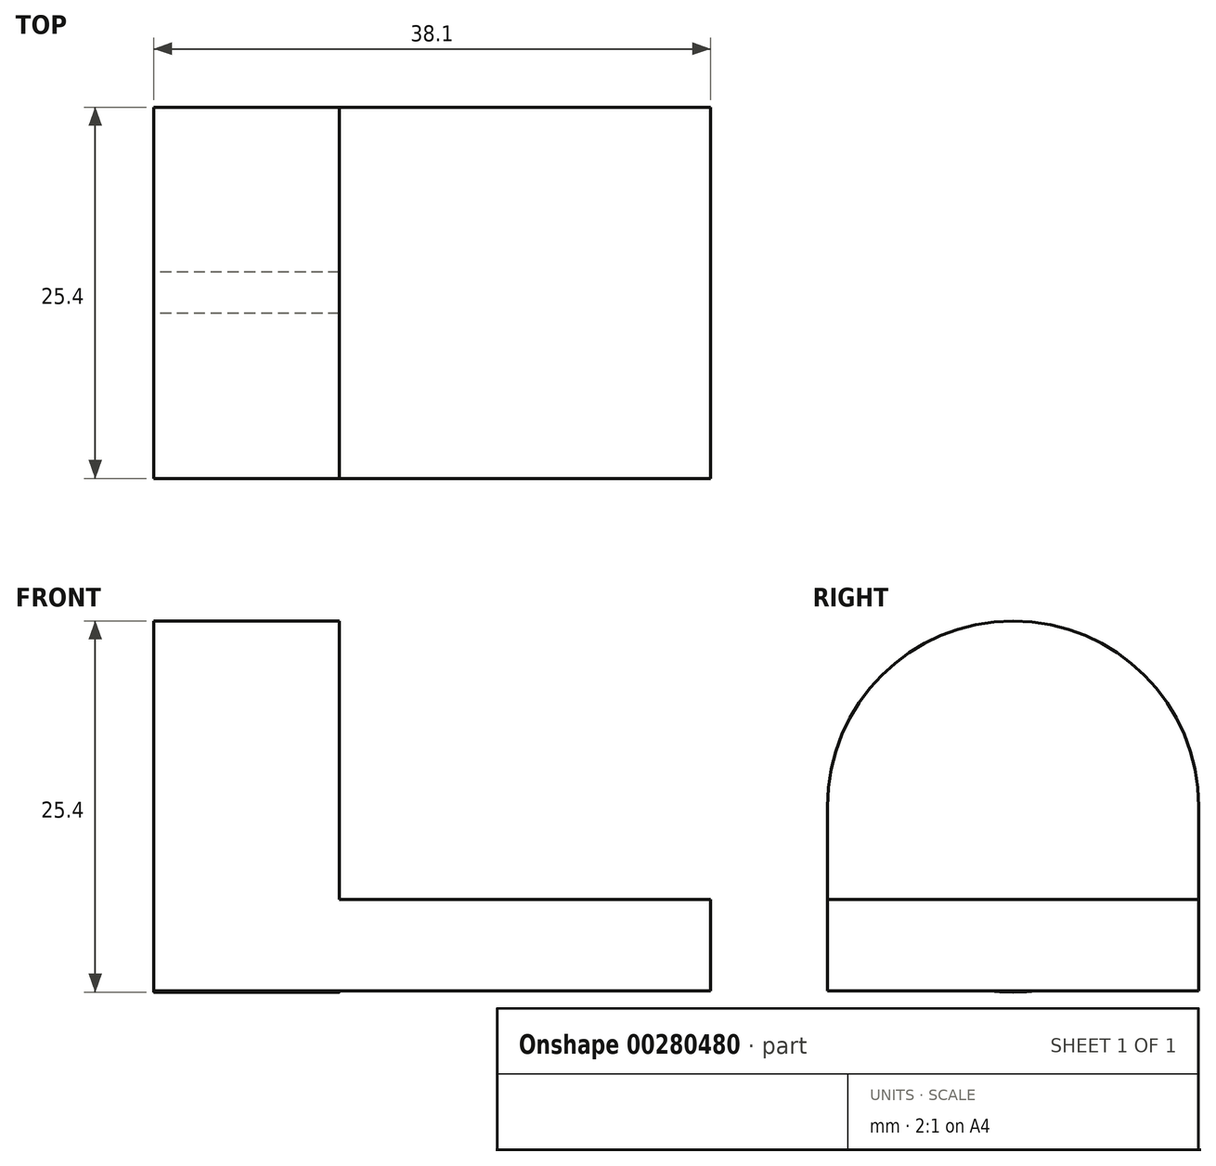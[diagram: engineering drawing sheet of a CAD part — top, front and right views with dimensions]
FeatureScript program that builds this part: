
annotation { "Feature Type Name" : "Feature", "Feature Type Description" : "" }
export const myFeature = defineFeature(function(context is Context, id is Id, definition is map)
    precondition{}
    {
        {
            var Q0;
            Q0=qCreatedBy(makeId("Right.planeOp"),FACE);
            var sketch = newSketch(context, id + "F0", { "sketchPlane" : qUnion([Q0])});
            skCircle(sketch, "E0", {"center": v(0, 12.62) * mm, "radius": 12.7 * mm});
            skSolve(sketch);
        }
        {
            var Q0;
            Q0 = qSketchRegion(id + "F0", true);
            extrude(context, id + "F1", {"entities" : qUnion([Q0]), "depth" : 12.7 * mm});
        }
        {
            var Q0;
            Q0=qCreatedBy(makeId("Right.planeOp"),FACE);
            var sketch = newSketch(context, id + "F2", { "sketchPlane" : qUnion([Q0])});
            skLineSegment(sketch, "E1.bottom", {"start": v(-12.7, 12.62) * mm, "end": v(12.7, 12.62) * mm});
            skLineSegment(sketch, "E1.top", {"start": v(-12.7, 0) * mm, "end": v(12.7, 0) * mm});
            skLineSegment(sketch, "E1.left", {"start": v(-12.7, 12.62) * mm, "end": v(-12.7, 0) * mm});
            skLineSegment(sketch, "E1.right", {"start": v(12.7, 12.62) * mm, "end": v(12.7, 0) * mm});
            skSolve(sketch);
        }
        {
            var Q0;
            Q0 = qSketchRegion(id + "F2", true);
            extrude(context, id + "F3", {"entities" : qUnion([Q0]), "operationType" : NewBodyOperationType.ADD, "depth" : 38.1 * mm});
        }
        {
            var Q0;
            Q0=qCreatedBy(makeId("Front.planeOp"),FACE);
            var sketch = newSketch(context, id + "F4", { "sketchPlane" : qUnion([Q0])});
            skLineSegment(sketch, "E2", {"start": v(12.7, 12.62) * mm, "end": v(12.7, 6.27) * mm});
            skLineSegment(sketch, "E3", {"start": v(12.7, 6.27) * mm, "end": v(38.1, 6.27) * mm});
            skLineSegment(sketch, "E4", {"start": v(38.1, 6.27) * mm, "end": v(38.1, 12.62) * mm});
            skLineSegment(sketch, "E5", {"start": v(38.1, 12.62) * mm, "end": v(12.7, 12.62) * mm});
            skSolve(sketch);
        }
        {
            var Q0;
            Q0 = qSketchRegion(id + "F4", true);
            extrude(context, id + "F5", {"entities" : qUnion([Q0]), "operationType" : NewBodyOperationType.REMOVE, "endBound" : BoundingType.SYMMETRIC, "depth" : 103.12 * mm});
        }
    });
